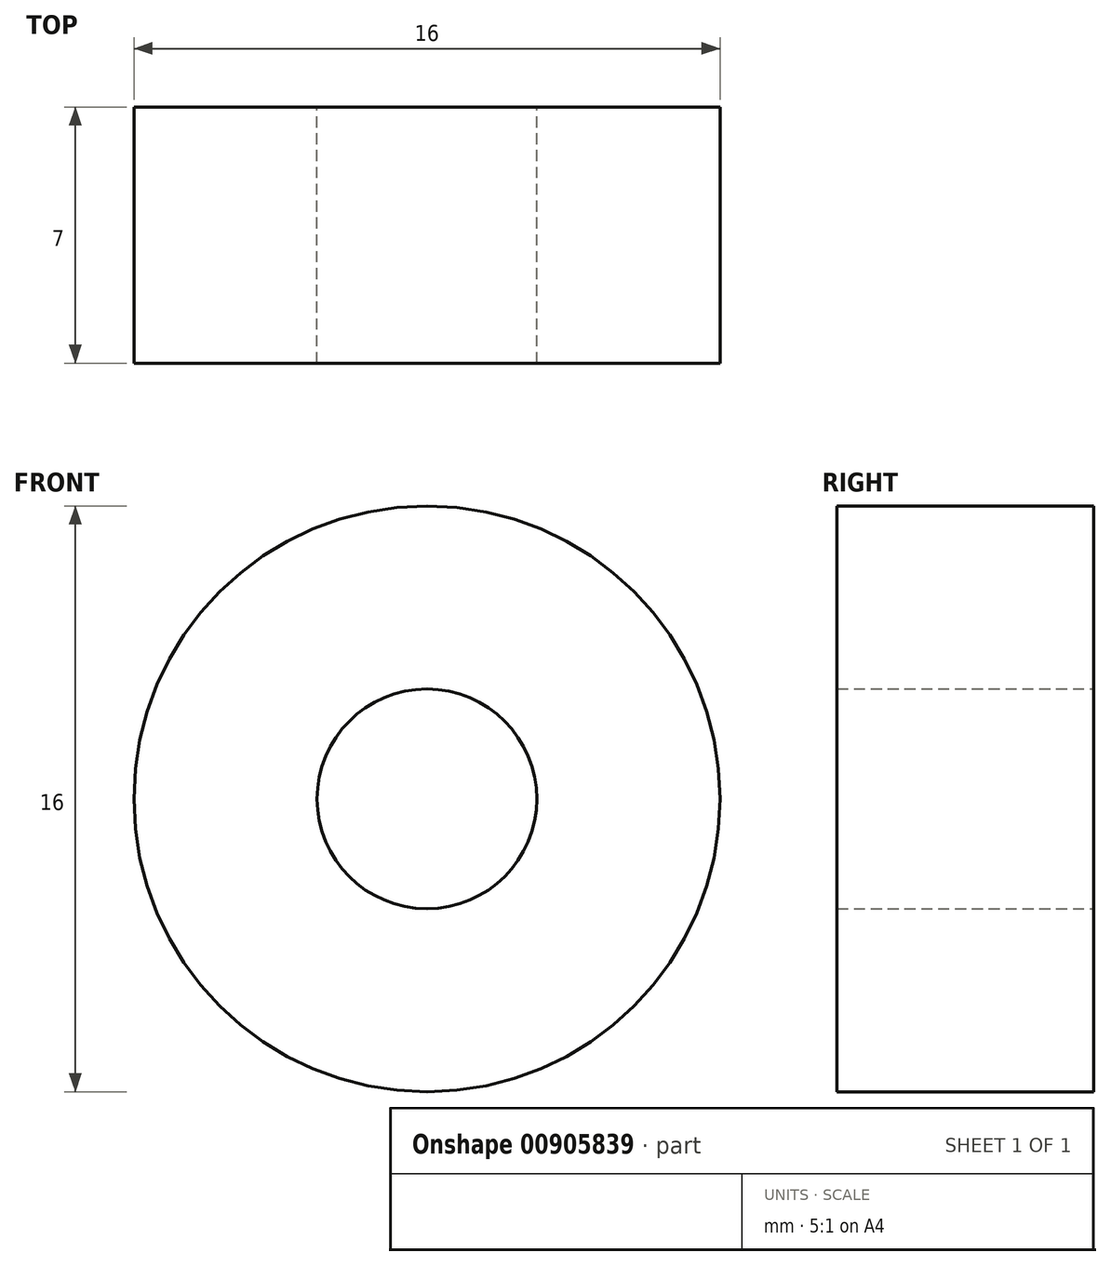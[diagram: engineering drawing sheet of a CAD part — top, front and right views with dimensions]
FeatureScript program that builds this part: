
annotation { "Feature Type Name" : "Feature", "Feature Type Description" : "" }
export const myFeature = defineFeature(function(context is Context, id is Id, definition is map)
    precondition{}
    {
        {
            var Q0;
            Q0=qCreatedBy(makeId("Front.planeOp"),FACE);
            var sketch = newSketch(context, id + "F0", { "sketchPlane" : qUnion([Q0])});
            skCircle(sketch, "E0", {"center": v(0, 0) * mm, "radius": 8 * mm});
            skCircle(sketch, "E1", {"center": v(0, 0) * mm, "radius": 3 * mm});
            skSolve(sketch);
        }
        {
            var Q0;
            Q0=makeQuery(id+"F0.imprint","IMPRINT",FACE,{"disambiguationData":[TD([[makeQuery(id+"F0.imprint","IMPRINT",EDGE,{"derivedFrom":sQuery(id+"F0.wireOp",EDGE,"E0")}),1.0]])]});
            extrude(context, id + "F1", {"entities" : qUnion([Q0]), "depth" : 7 * mm, "offsetDistance" : 25 * mm, "symmetric" : true});
        }
    });
